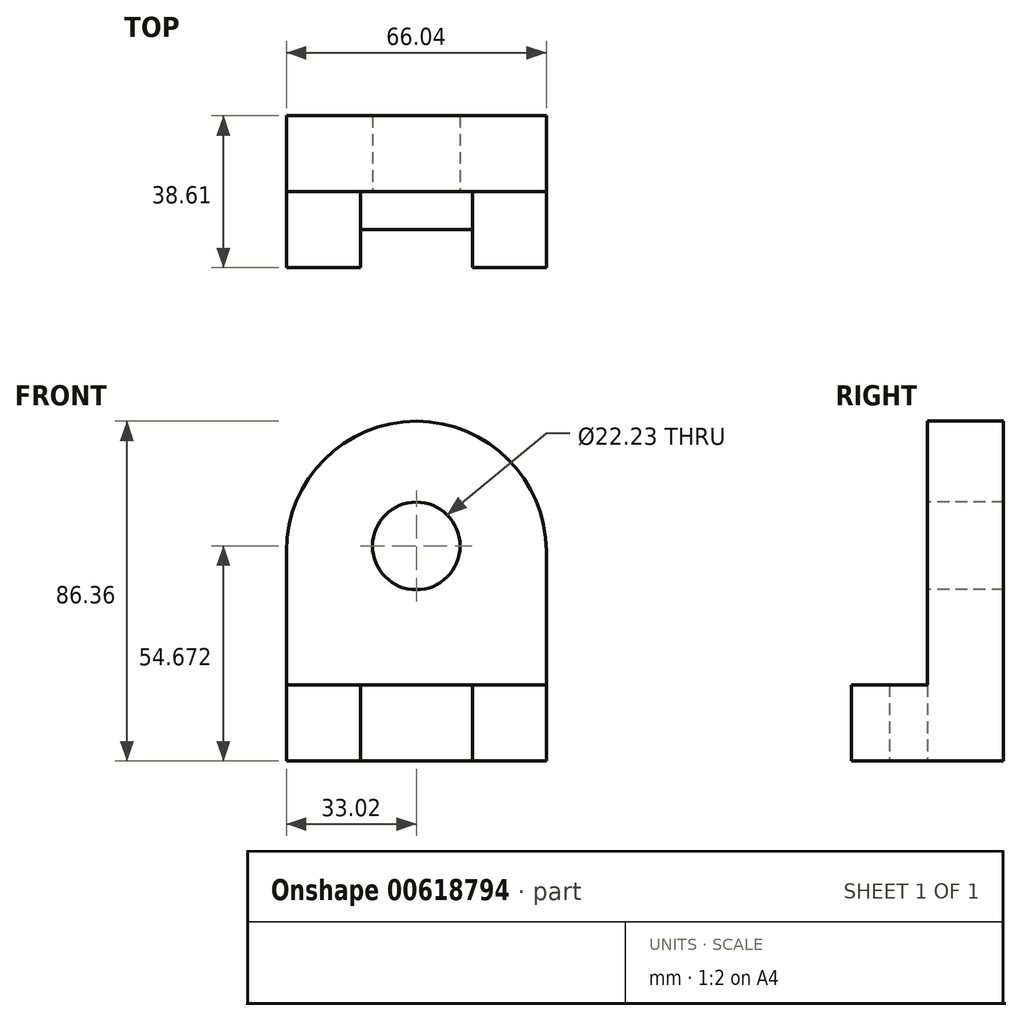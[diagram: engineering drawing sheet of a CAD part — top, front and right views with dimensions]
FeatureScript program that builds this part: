
annotation { "Feature Type Name" : "Feature", "Feature Type Description" : "" }
export const myFeature = defineFeature(function(context is Context, id is Id, definition is map)
    precondition{}
    {
        {
            var Q0;
            Q0=qCreatedBy(makeId("Front.planeOp"),FACE);
            var sketch = newSketch(context, id + "F0", { "sketchPlane" : qUnion([Q0])});
            skLineSegment(sketch, "E0", {"start": v(0, 0) * mm, "end": v(0, 53.34) * mm});
            skLineSegment(sketch, "E1", {"start": v(0, 53.34) * mm, "end": v(66.04, 53.34) * mm});
            skLineSegment(sketch, "E2", {"start": v(66.04, 53.34) * mm, "end": v(66.04, 0) * mm});
            skLineSegment(sketch, "E3", {"start": v(66.04, 0) * mm, "end": v(0, 0) * mm});
            skArc(sketch, "E4", {"start": v(66.04, 53.34) * mm, "mid": v(33.02, 86.36) * mm, "end": v(0, 53.34) * mm});
            skSolve(sketch);
        }
        {
            var Q0;
            Q0 = qSketchRegion(id + "F0", true);
            extrude(context, id + "F1", {"entities" : qUnion([Q0]), "depth" : 19.3 * mm, "offsetDistance" : 25.4 * mm});
        }
        {
            var Q0;
            Q0=makeQuery(id+"F1.opExtrude","CAP_FACE",FACE,{"disambiguationData":[OSD([sQuery(id+"F0.wireOp",EDGE,"E0"),sQuery(id+"F0.wireOp",EDGE,"E2"),sQuery(id+"F0.wireOp",EDGE,"E3"),sQuery(id+"F0.wireOp",EDGE,"E4")])],"isStart":false});
            var sketch = newSketch(context, id + "F2", { "sketchPlane" : qUnion([Q0])});
            skLineSegment(sketch, "E5", {"start": v(0, 19.3) * mm, "end": v(66.04, 19.3) * mm});
            skLineSegment(sketch, "E6", {"start": v(66.04, 19.3) * mm, "end": v(66.04, 0) * mm});
            skLineSegment(sketch, "E7", {"start": v(66.04, 0) * mm, "end": v(0, 0) * mm});
            skLineSegment(sketch, "E8", {"start": v(0, 0) * mm, "end": v(0, 19.3) * mm});
            skLineSegment(sketch, "E9", {"start": v(18.8, 19.3) * mm, "end": v(18.8, 0) * mm});
            skLineSegment(sketch, "E10", {"start": v(47.24, 19.3) * mm, "end": v(47.24, 0) * mm});
            skSolve(sketch);
        }
        {
            var Q0;
            {var subQ0=sQuery(id+"F2.wireOp",EDGE,"E8");Q0=makeQuery(id+"F2.imprint","IMPRINT",FACE,{"disambiguationData":[TD([[makeQuery(id+"F2.imprint","IMPRINT",EDGE,{"derivedFrom":subQ0}),-1.0]])]});}
            var Q1;
            {var subQ0=sQuery(id+"F2.wireOp",EDGE,"E6");Q1=makeQuery(id+"F2.imprint","IMPRINT",FACE,{"disambiguationData":[TD([[makeQuery(id+"F2.imprint","IMPRINT",EDGE,{"derivedFrom":subQ0}),-1.0]])]});}
            extrude(context, id + "F3", {"entities" : qUnion([Q0, Q1]), "operationType" : NewBodyOperationType.ADD, "depth" : 19.3 * mm, "offsetDistance" : 25.4 * mm});
        }
        {
            var Q0;
            {var subQ0=sQuery(id+"F2.wireOp",EDGE,"E9");Q0=makeQuery(id+"F2.imprint","IMPRINT",FACE,{"disambiguationData":[TD([[makeQuery(id+"F2.imprint","IMPRINT",EDGE,{"derivedFrom":subQ0}),1.0]])]});}
            extrude(context, id + "F4", {"entities" : qUnion([Q0]), "depth" : 9.65 * mm, "offsetDistance" : 25.4 * mm});
        }
        {
            var Q0;
            {var subQ5=makeQuery(id+"F1.opExtrude","CAP_EDGE",EDGE,{"disambiguationData":[OSD([sQuery(id+"F0.wireOp",EDGE,"E4")])],"isStart":false});Q0=makeQuery(id+"F2.imprint","IMPRINT",FACE,{"disambiguationData":[TD([[makeQuery(id+"F2.imprint","IMPRINT",EDGE,{"derivedFrom":subQ5}),1.0]])]});}
            var sketch = newSketch(context, id + "F5", { "sketchPlane" : qUnion([Q0])});
            skCircle(sketch, "E11", {"center": v(33.02, 54.67) * mm, "radius": 11.11 * mm});
            skSolve(sketch);
        }
        {
            var Q0;
            Q0=sQuery(id+"F5.wireOp",VERTEX,"E11.center");
            var Q1;
            Q1=makeQuery(id+"F1.opExtrude","SWEPT_BODY",BODY,{"disambiguationData":[OSD([sQuery(id+"F0.wireOp",EDGE,"E0"),sQuery(id+"F0.wireOp",EDGE,"E2"),sQuery(id+"F0.wireOp",EDGE,"E3"),sQuery(id+"F0.wireOp",EDGE,"E4")])]});
            hole(context, id + "F6", {"style" : HoleStyle.SIMPLE, "endStyle" : HoleEndStyle.THROUGH, "holeDiameter" : 22.22 * mm, "majorDiameter" : 6.35 * mm, "isTappedThrough" : true, "tappedDepth" : 12.7 * mm, "tapClearance" : 3, "locations" : qUnion([Q0]), "scope" : qUnion([Q1])});
        }
    });
